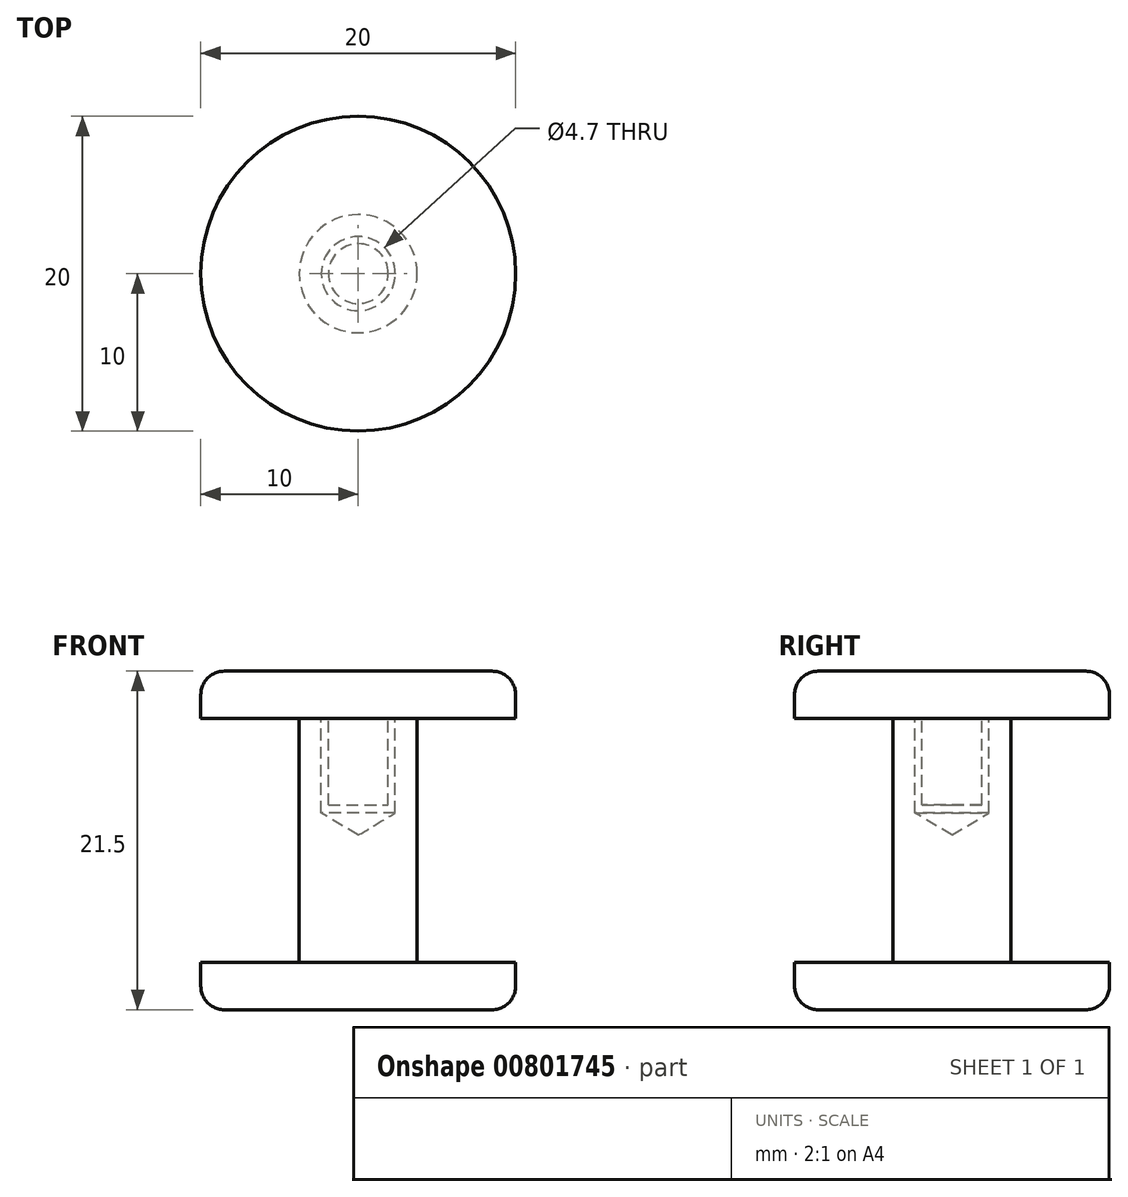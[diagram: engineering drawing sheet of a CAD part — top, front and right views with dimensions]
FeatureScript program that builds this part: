
annotation { "Feature Type Name" : "Feature", "Feature Type Description" : "" }
export const myFeature = defineFeature(function(context is Context, id is Id, definition is map)
    precondition{}
    {
        {
            var Q0;
            Q0=qCreatedBy(makeId("Top.planeOp"),FACE);
            var sketch = newSketch(context, id + "F0", { "sketchPlane" : qUnion([Q0])});
            skCircle(sketch, "E0", {"center": v(0, 0) * mm, "radius": 10 * mm});
            skSolve(sketch);
        }
        {
            var Q0;
            Q0 = qSketchRegion(id + "F0", true);
            extrude(context, id + "F1", {"entities" : qUnion([Q0]), "depth" : 3 * mm, "offsetDistance" : 25 * mm});
        }
        {
            var Q0;
            Q0=makeQuery(id+"F1.opExtrude","CAP_FACE",FACE,{"disambiguationData":[OSD([sQuery(id+"F0.wireOp",EDGE,"E0")])],"isStart":false});
            var sketch = newSketch(context, id + "F2", { "sketchPlane" : qUnion([Q0])});
            skCircle(sketch, "E1", {"center": v(0, 0) * mm, "radius": 3.75 * mm});
            skSolve(sketch);
        }
        {
            var Q0;
            Q0 = qSketchRegion(id + "F2", true);
            extrude(context, id + "F3", {"entities" : qUnion([Q0]), "operationType" : NewBodyOperationType.ADD, "depth" : 15.5 * mm, "offsetDistance" : 25 * mm});
        }
        {
            var Q0;
            Q0=makeQuery(id+"F3.opExtrude","CAP_FACE",FACE,{"disambiguationData":[OSD([sQuery(id+"F2.wireOp",EDGE,"E1")])],"isStart":false});
            var sketch = newSketch(context, id + "F4", { "sketchPlane" : qUnion([Q0])});
            skPoint(sketch, "E2", {"position": v(0, 0) * mm});
            skSolve(sketch);
        }
        {
            var Q0;
            Q0=sQuery(id+"F4.wireOp",VERTEX,"E2");
            var Q1;
            Q1=makeQuery(id+"F1.opExtrude","SWEPT_BODY",BODY,{"disambiguationData":[OSD([sQuery(id+"F0.wireOp",EDGE,"E0")])]});
            hole(context, id + "F5", {"style" : HoleStyle.SIMPLE, "endStyle" : HoleEndStyle.BLIND, "holeDiameter" : 4.7 * mm, "majorDiameter" : 5 * mm, "holeDepth" : 6 * mm, "isTappedThrough" : true, "tappedDepth" : 12 * mm, "tapClearance" : 3, "locations" : qUnion([Q0]), "scope" : qUnion([Q1])});
        }
        {
            var Q0;
            Q0=makeQuery(id+"F1.opExtrude","CAP_EDGE",EDGE,{"disambiguationData":[OSD([sQuery(id+"F0.wireOp",EDGE,"E0")])],"isStart":true});
            fillet(context, id + "F6", {"entities" : qUnion([Q0]), "radius" : 1.5 * mm, "tangentPropagation" : true, "allowEdgeOverflow" : false});
        }
        {
            var Q0;
            Q0=makeQuery(id+"F3.opExtrude","CAP_FACE",FACE,{"disambiguationData":[OSD([sQuery(id+"F2.wireOp",EDGE,"E1")])],"isStart":false});
            var sketch = newSketch(context, id + "F7", { "sketchPlane" : qUnion([Q0])});
            skCircle(sketch, "E3", {"center": v(0, 0) * mm, "radius": 10 * mm});
            skSolve(sketch);
        }
        {
            var Q0;
            Q0 = qSketchRegion(id + "F7", true);
            extrude(context, id + "F8", {"entities" : qUnion([Q0]), "depth" : 3 * mm, "offsetDistance" : 25 * mm});
        }
        {
            var Q0;
            Q0=makeQuery(id+"F8.opExtrude","CAP_FACE",FACE,{"disambiguationData":[OSD([sQuery(id+"F7.wireOp",EDGE,"E3")])],"isStart":true});
            var sketch = newSketch(context, id + "F9", { "sketchPlane" : qUnion([Q0])});
            skCircle(sketch, "E4", {"center": v(0, 0) * mm, "radius": 1.9 * mm});
            skSolve(sketch);
        }
        {
            var Q0;
            Q0 = qSketchRegion(id + "F9", true);
            extrude(context, id + "F10", {"entities" : qUnion([Q0]), "operationType" : NewBodyOperationType.ADD, "depth" : 5.5 * mm, "offsetDistance" : 25 * mm});
        }
        {
            var Q0;
            Q0=makeQuery(id+"F8.opExtrude","CAP_EDGE",EDGE,{"disambiguationData":[OSD([sQuery(id+"F7.wireOp",EDGE,"E3")])],"isStart":false});
            fillet(context, id + "F11", {"entities" : qUnion([Q0]), "radius" : 1.5 * mm, "tangentPropagation" : true, "allowEdgeOverflow" : false});
        }
    });
